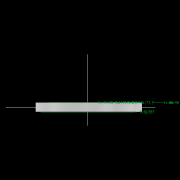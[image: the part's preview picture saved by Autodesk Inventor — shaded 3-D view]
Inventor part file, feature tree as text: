
AUTODESK INVENTOR PART (.ipt)
format: ipt  version: 2022.2 (Build 262287010, 287A)  size: 844,800 bytes
history: native  units: mm
features: extrude x19, sketch x18, pattern_circular x15, other x14, revolve x7, hole x7, move_body x4, fillet x2, draft x2
ambient origin geometry x8: Origin, YZ Plane, XZ Plane, XY Plane, X Axis, Y Axis, Z Axis, Center Point
bodies: Solid1 (feature_tree), Solid2 (feature_tree), Solid3 (feature_tree), Solid4 (feature_tree), Solid5 (feature_tree)
feature tree (88):
  sketch  "Sketch7"  dims[d21=0.5mm]
  other  "Roller1"
  other  "Roller2"
  sketch  "Sketch22"  dims[d39=0.05mm]
  sketch  "Sketch2"  dims[d17=0.05mm]
  sketch  "Sketch23"  dims[d41=0.05mm]
  other  "RevRoller1"
  fillet  "Fillet1"  Radius=0.05mm
  pattern_circular  "Circular Pattern13"  Count=6  [1 undecoded]
  move_body  "Move Body7"
  revolve  "Revolution13"  Angle=30.0deg
  fillet  "Fillet3"  [1 undecoded]
  pattern_circular  "Circular Pattern14"  [2 undecoded]
  move_body  "Move Body6"
  revolve  "Revolution14"  [1 undecoded]
  other  "OuterRim_Top2"
  other  "OuterRim_Bottom2"
  extrude  "Extrusion9"  TaperAngle=90.0deg  [1 undecoded]
  sketch  "Sketch24"  dims[d42=0.5mm]
  extrude  "Extrusion10"  Depth=3.0mm
  extrude  "Extrusion11"  Depth=3.0mm
  pattern_circular  "Circular Pattern15"  [2 undecoded]
  sketch  "Sketch25"  dims[d43=0.5mm]
  extrude  "Extrusion12"  Depth=3.0mm
  extrude  "Extrusion14"  Depth=3.0mm
  extrude  "Extrusion15"  Depth=3.0mm
  pattern_circular  "Circular Pattern16"  [2 undecoded]
  extrude  "Extrusion16"  Depth=3.0mm
  extrude  "Extrusion17"  Depth=3.0mm
  hole  "Hole9"  [1 undecoded]
  pattern_circular  "Circular Pattern17"  [2 undecoded]
  sketch  "Sketch27"  dims[d45=0.5mm]
  hole  "Hole10"  [1 undecoded]
  hole  "Hole11"  [1 undecoded]
  pattern_circular  "Circular Pattern18"  [2 undecoded]
  extrude  "Extrusion18"  Depth=3.0mm
  extrude  "Extrusion19"  Depth=3.0mm
  pattern_circular  "Circular Pattern19"  [2 undecoded]
  sketch  "Sketch28"  dims[d46=0.5mm d47=0.5mm d48=2.0mm d50=90.0deg d56=14.029612mm d57=4.025mm d90=16.473921mm d107=0.05mm d108=0.05mm d109=0.05mm d110=0.05mm d112=0.5mm d113=0.5mm d114=0.5mm d115=14.644822mm d116=14.607374mm d117=1.0mm d118=0.05mm d119=0.05mm d120=0.05mm d121=0.05mm d122=0.5mm d123=0.5mm d124=14.644822mm d125=14.607374mm d126=1.0mm d127=90.0deg d128=30.0deg d129=90.0deg d167=8.972256mm d173=10.814812mm d201=53.5mm d202=90.0deg d203=90.0deg d204=90.0deg d218=53.5mm d226=5.4mm d232=0.0mm d233=3600.0mm d234=10.502mm d235=0.0mm d243=1.902mm d244=0.0mm d246=2.75mm d247=5.251mm d248=0.0mm d249=3.0mm d250=0.0mm d251=90.0mm d252=360.0deg d254=2.75mm d255=3.0mm d256=5.251mm d257=0.0mm d258=3.0mm d259=0.0mm d260=90.0mm d261=360.0deg d277=76.5mm d281=73.5mm d282=24.65mm d283=6.0mm d284=4.0mm d285=2.0mm d286=90.0deg d287=5.251mm d288=0.0mm d289=60.0mm d290=360.0deg d292=0.436332mm d293=60.0mm d294=90.0mm d295=3.0mm d296=6.0mm d297=5.5mm d298=3.0mm d299=90.0deg d300=5.251mm d301=0.0mm d302=60.0mm d303=360.0deg d305=30.0deg d306=73.5mm d307=24.65mm d308=6.0mm d309=5.5mm d310=3.0mm d311=90.0deg d312=5.251mm d313=0.0mm d314=60.0mm d315=360.0deg d317=90.0mm d318=60.0mm d319=30.0deg d320=5.4mm d321=5.4mm d322=3.0mm d323=6.0mm d324=5.5mm d325=3.0mm d326=90.0deg d327=5.251mm d328=0.0mm d329=2.4mm d330=0.0mm d331=60.0mm d332=360.0deg d343=17.307186mm d344=17.309884mm d345=0.025mm d346=0.025mm d347=0.1mm d348=0.1mm d349=17.309884mm d350=17.307186mm d351=0.025mm d352=0.025mm d354=0.1mm d355=17.307186mm d356=17.309884mm d357=1.0mm d358=90.0deg d359=0.5mm d360=60.0mm d361=360.0deg d363=30.0deg d367=8.1mm d369=4.014775mm d370=0.1mm d371=1.0mm d372=30.0deg d373=90.0deg d374=0.5mm d375=60.0mm d376=360.0deg d378=90.0deg d379=0.1mm d380=0.1mm d381=0.1mm d382=0.1mm d383=0.1mm d384=10.502mm d385=0.0mm d386=0.0mm d391=1.0mm d392=53.5mm d393=1.5mm d394=1.5mm d395=1.5mm d396=1.5mm d397=90.0deg d398=90.0deg d399=90.0deg d400=53.5mm d401=10.502mm d402=0.0mm d403=2.75mm d404=1.5mm d405=10.502mm d406=0.0mm d407=3.0mm d408=0.0mm d409=90.0mm d410=360.0deg d412=5.4mm d413=5.251mm d414=0.0mm d417=5.4mm d418=2.4mm d419=0.0mm d420=2.4mm d421=0.0mm d422=90.0mm d423=360.0deg d425=60.0mm d426=90.0mm d427=1.5mm d428=1.5mm d429=5.4mm d430=5.4mm d431=5.251mm d432=0.0mm d433=2.4mm d434=0.0mm d435=30.0deg d436=73.5mm d437=24.65mm d438=6.0mm d439=4.0mm d440=2.0mm d441=90.0deg d442=5.251mm d443=0.0mm d444=60.0mm d445=360.0deg d447=3.0mm d448=6.0mm d449=5.5mm d450=3.0mm d451=90.0deg d452=5.251mm d453=0.0mm d454=24.65mm d455=6.0mm d456=5.5mm d457=3.0mm d458=90.0deg d459=5.251mm d460=0.0mm d461=60.0mm d462=360.0deg d464=5.251mm d465=0.0mm d466=3.0mm d467=0.0mm d468=90.0mm d469=360.0deg d472=1.5mm d474=5.251mm d475=0.0mm d481=3.0mm d482=0.0mm d483=90.0mm d484=360.0deg d486=0.436332mm d49=0.872665mm d51=0.872665mm d52=0.872665mm d236=0.5mm d237=0.872665mm d238=0.5mm d239=0.872665mm d291=0.0625mm d415=0.5mm d416=0.872665mm d471=0.5mm d473=0.5mm]
  extrude  "Extrusion20"  Depth=3.0mm
  extrude  "Extrusion22"  Depth=3.0mm
  pattern_circular  "Circular Pattern21"  [2 undecoded]
  draft  "FaceDraft2"
  other  "InnerRim"
  other  "OuterRim_Top"
  other  "OuterRim_Bottom"
  extrude  "Extrusion2"  Depth=3.0mm
  sketch  "Sketch13"  dims[d24=0.5mm]
  extrude  "Extrusion3"  Depth=3.0mm
  sketch  "Sketch15"  dims[d29=360.0deg d30=60.0mm]
  extrude  "Extrusion4"  TaperAngle=90.0deg  [1 undecoded]
  extrude  "Extrusion5"  TaperAngle=30.0deg  [1 undecoded]
  pattern_circular  "Circular Pattern6"  Angle=90.0deg  [1 undecoded]
  sketch  "Sketch16"  dims[d31=360.0deg d35=30.0deg d36=90.0deg]
  extrude  "Extrusion6"  Depth=3.0mm
  extrude  "Extrusion7"  Depth=3.0mm
  pattern_circular  "Circular Pattern7"  [2 undecoded]
  hole  "Hole5"  [1 undecoded]
  pattern_circular  "Circular Pattern9"  Angle=90.0deg  [1 undecoded]
  draft  "FaceDraft1"
  hole  "Hole6"  [1 undecoded]
  pattern_circular  "Circular Pattern10"  [2 undecoded]
  hole  "Hole7"  [1 undecoded]
  pattern_circular  "Circular Pattern11"  Count=360  [1 undecoded]
  hole  "Hole8"  [1 undecoded]
  extrude  "Extrusion8"  TaperAngle=0.0deg  [1 undecoded]
  pattern_circular  "Circular Pattern12"  [2 undecoded]
  sketch  "Sketch8"  dims[d22=0.5mm]
  sketch  "Sketch9"  dims[d23=0.5mm]
  revolve  "Revolution4"  [1 undecoded]
  move_body  "Move Body4"
  revolve  "Revolution5"  [1 undecoded]
  sketch  "Sketch5"  dims[d19=0.5mm]
  sketch  "Sketch6"  dims[d20=0.5mm]
  revolve  "Revolution3"  [1 undecoded]
  sketch  "Sketch4"  dims[d18=0.05mm]
  revolve  "Revolution1"  [1 undecoded]
  pattern_circular  "Circular Pattern1"  [2 undecoded]
  move_body  "Move Body3"
  revolve  "Revolution2"  [1 undecoded]
  other  "2D Equation Curve1"
  sketch  "Sketch14"  dims[d28=2.0mm]
  other  "Work Axis1"
  other  "Work Axis2"
  other  "Work Axis3"
  other  "Work Axis4"
  other  "Work Axis5"
  sketch  "Sketch26"  dims[d44=0.5mm]
note: 44 required parameter values undecoded (feature->parameter linkage not recoverable at this tier; creation-order binding heuristic only, values carry confidence <= 0.55)